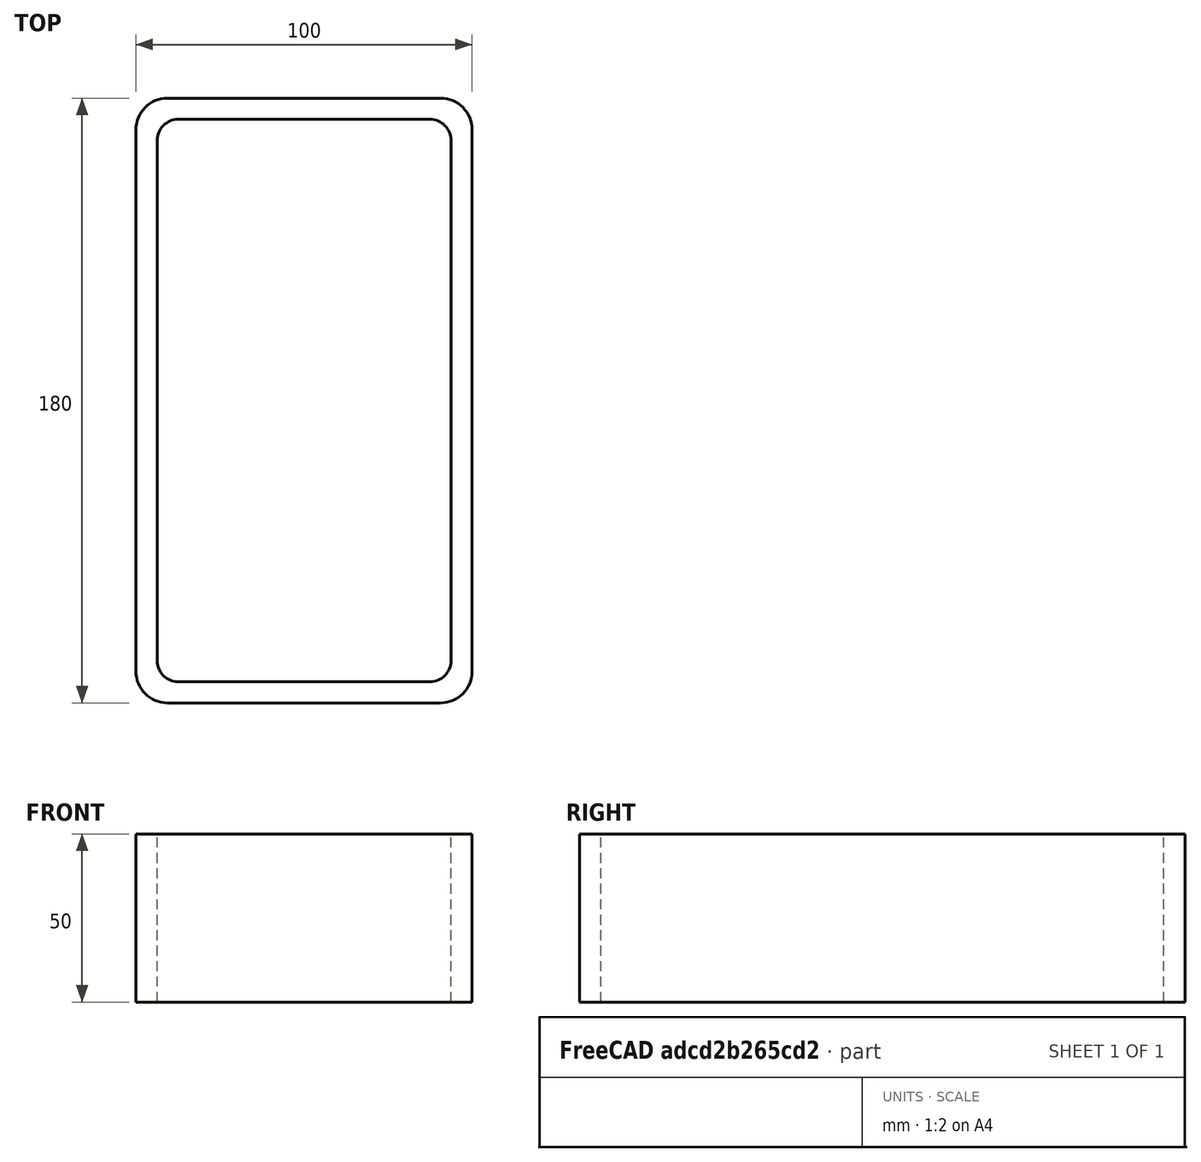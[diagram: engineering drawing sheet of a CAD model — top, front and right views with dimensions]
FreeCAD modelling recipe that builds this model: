
FCSTD DOCUMENT  (FreeCAD 0.15R4671 (Git))
Label: Rectangular hollow section 180x100x6.3 EN10219 S235JRH
License: All rights reserved
LicenseURL: http://en.wikipedia.org/wiki/All_rights_reserved
objects: Sketcher::SketchObject×1, Part::Extrusion×1
note: 2 computed .brp shape members not serialized (recipe doc carries the construction recipe); baked Part::Feature solids carry a one-line shape summary decoded from their .brp

FEATURE [Sketcher::SketchObject] Sketch
  sketch-geometry (16):
    g0: LineSegment StartX=-37.4 StartY=83.7 StartZ=0 EndX=37.4 EndY=83.7 EndZ=0
    g1: LineSegment StartX=43.7 StartY=77.4 StartZ=0 EndX=43.7 EndY=-77.4 EndZ=0
    g2: LineSegment StartX=37.4 StartY=-83.7 StartZ=0 EndX=-37.4 EndY=-83.7 EndZ=0
    g3: LineSegment StartX=-43.7 StartY=-77.4 StartZ=0 EndX=-43.7 EndY=77.4 EndZ=0
    g4: LineSegment StartX=-40.55 StartY=90 StartZ=0 EndX=40.55 EndY=90 EndZ=0
    g5: LineSegment StartX=50 StartY=80.55 StartZ=0 EndX=50 EndY=-80.55 EndZ=0
    g6: LineSegment StartX=40.55 StartY=-90 StartZ=0 EndX=-40.55 EndY=-90 EndZ=0
    g7: LineSegment StartX=-50 StartY=-80.55 StartZ=0 EndX=-50 EndY=80.55 EndZ=0
    g8: ArcOfCircle CenterX=-37.4 CenterY=77.4 CenterZ=0 NormalX=0 NormalY=0 NormalZ=1 Radius=6.3 StartAngle=1.5708 EndAngle=3.14159
    g9: ArcOfCircle CenterX=37.4 CenterY=77.4 CenterZ=0 NormalX=0 NormalY=0 NormalZ=1 Radius=6.3 StartAngle=0 EndAngle=1.5708
    g10: ArcOfCircle CenterX=37.4 CenterY=-77.4 CenterZ=0 NormalX=0 NormalY=0 NormalZ=1 Radius=6.3 StartAngle=4.71239 EndAngle=6.28319
    g11: ArcOfCircle CenterX=-37.4 CenterY=-77.4 CenterZ=0 NormalX=0 NormalY=0 NormalZ=1 Radius=6.3 StartAngle=3.14159 EndAngle=4.71239
    g12: ArcOfCircle CenterX=40.55 CenterY=80.55 CenterZ=0 NormalX=0 NormalY=0 NormalZ=1 Radius=9.45 StartAngle=0 EndAngle=1.5708
    g13: ArcOfCircle CenterX=40.55 CenterY=-80.55 CenterZ=0 NormalX=0 NormalY=0 NormalZ=1 Radius=9.45 StartAngle=4.71239 EndAngle=6.28319
    g14: ArcOfCircle CenterX=-40.55 CenterY=-80.55 CenterZ=0 NormalX=0 NormalY=0 NormalZ=1 Radius=9.45 StartAngle=3.14159 EndAngle=4.71239
    g15: ArcOfCircle CenterX=-40.55 CenterY=80.55 CenterZ=0 NormalX=0 NormalY=0 NormalZ=1 Radius=9.45 StartAngle=1.5708 EndAngle=3.14159
  constraints (36):
    c: Horizontal(g2)
    c: Vertical(g3)
    c: Horizontal(g6)
    c: Vertical(g7)
    c: Tangent(g3,g8) = 1.5708
    c: Tangent(g0,g8) = 1.5708
    c: Tangent(g0,g9) = 1.5708
    c: Tangent(g1,g9) = 1.5708
    c: Tangent(g1,g10) = 1.5708
    c: Tangent(g2,g10) = 1.5708
    c: Tangent(g2,g11) = 1.5708
    c: Tangent(g3,g11) = 1.5708
    c: Tangent(g4,g12) = 1.5708
    c: Tangent(g5,g12) = 1.5708
    c: Tangent(g5,g13) = 1.5708
    c: Tangent(g6,g13) = 1.5708
    c: Tangent(g6,g14) = 1.5708
    c: Tangent(g7,g14) = 1.5708
    c: Tangent(g7,g15) = 1.5708
    c: Tangent(g4,g15) = 1.5708
    c: Equal(g9,g8)
    c: Equal(g9,g11)
    c: Equal(g9,g10)
    c: Equal(g12,g15)
    c: Equal(g12,g14)
    c: Equal(g12,g13)
    c: Symmetric(g4,g6,g-1)
    c: Symmetric(g7,g5,g-2)
    c: DistanceY(g4,g6) = -180
    c: DistanceX(g7,g5) = 100
    c: Symmetric(g3,g1,g-2)
    c: Symmetric(g0,g2,g-1)
    c: DistanceY(g0,g4) = 6.3
    c: DistanceX(g5,g1) = -6.3
    c: Radius(g9) = 6.3
    c: Radius(g12) = 9.45
FEATURE [Part::Extrusion] Extrude  label="Rectangular hollow section 180x100x6.3 EN10219 S235JRH"
  Base = -> Sketch
  Dir = (0,0,50)
  Solid = true
